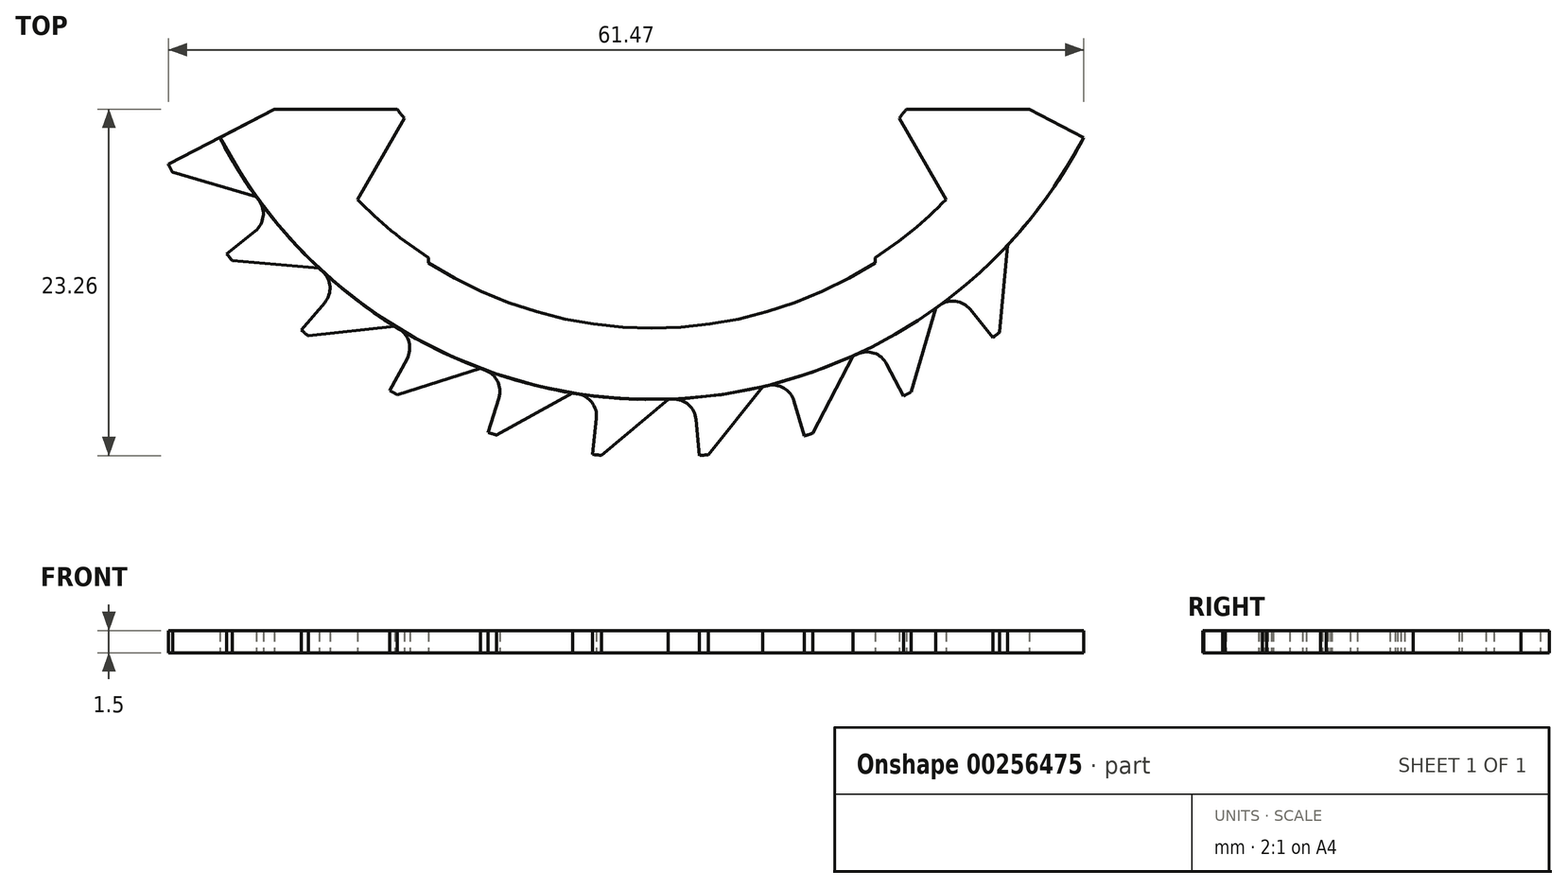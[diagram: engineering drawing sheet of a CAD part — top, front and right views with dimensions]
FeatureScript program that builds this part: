
annotation { "Feature Type Name" : "Feature", "Feature Type Description" : "" }
export const myFeature = defineFeature(function(context is Context, id is Id, definition is map)
    precondition{}
    {
        {
            var Q0;
            Q0=qCreatedBy(makeId("Top.planeOp"),FACE);
            var sketch = newSketch(context, id + "F0", { "sketchPlane" : qUnion([Q0]), "disableImprinting" : false});
            skArc(sketch, "E0", {"start": v(5, -7.72) * mm, "mid": v(5.83, -7.12) * mm, "end": v(6.6, -6.42) * mm});
            skArc(sketch, "E1", {"start": v(-5, -7.84) * mm, "mid": v(0, -9.3) * mm, "end": v(5, -7.84) * mm});
            skArc(sketch, "E2", {"start": v(7.64, -9.51) * mm, "mid": v(7.71, -9.45) * mm, "end": v(7.8, -9.39) * mm});
            skCircle(sketch, "E3", {"center": v(0, 0) * mm, "radius": 10.9 * mm});
            skLineSegment(sketch, "E4", {"start": v(0, 0) * mm, "end": v(-10.82, -5.63) * mm});
            skLineSegment(sketch, "E5", {"start": v(0, 0) * mm, "end": v(9.67, -5.03) * mm});
            skLineSegment(sketch, "E6", {"start": v(0, 0) * mm, "end": v(7.64, -9.51) * mm, "construction": true});
            skLineSegment(sketch, "E7", {"start": v(6.82, -8.5) * mm, "end": v(7.64, -9.51) * mm});
            skLineSegment(sketch, "E8", {"start": v(7.8, -9.39) * mm, "end": v(7.96, -7.45) * mm});
            skLineSegment(sketch, "E9", {"start": v(0, 0) * mm, "end": v(9.35, -7.84) * mm, "construction": true});
            skLineSegment(sketch, "E10.1.0", {"start": v(5.8, -10.73) * mm, "end": v(6.36, -8.86) * mm});
            skArc(sketch, "E10.1.1", {"start": v(5.63, -10.82) * mm, "mid": v(5.72, -10.77) * mm, "end": v(5.8, -10.73) * mm});
            skLineSegment(sketch, "E10.1.2", {"start": v(5.03, -9.67) * mm, "end": v(5.63, -10.82) * mm});
            skLineSegment(sketch, "E10.2.0", {"start": v(3.6, -11.66) * mm, "end": v(4.5, -9.92) * mm});
            skArc(sketch, "E10.2.1", {"start": v(3.41, -11.71) * mm, "mid": v(3.5, -11.68) * mm, "end": v(3.6, -11.66) * mm});
            skLineSegment(sketch, "E10.2.2", {"start": v(3.05, -10.46) * mm, "end": v(3.41, -11.71) * mm});
            skLineSegment(sketch, "E10.3.0", {"start": v(1.26, -12.13) * mm, "end": v(2.48, -10.61) * mm});
            skArc(sketch, "E10.3.1", {"start": v(1.06, -12.15) * mm, "mid": v(1.16, -12.14) * mm, "end": v(1.26, -12.13) * mm});
            skLineSegment(sketch, "E10.3.2", {"start": v(0.95, -10.86) * mm, "end": v(1.06, -12.15) * mm});
            skLineSegment(sketch, "E10.4.0", {"start": v(-1.13, -12.15) * mm, "end": v(0.36, -10.9) * mm});
            skArc(sketch, "E10.4.1", {"start": v(-1.33, -12.13) * mm, "mid": v(-1.23, -12.14) * mm, "end": v(-1.13, -12.15) * mm});
            skLineSegment(sketch, "E10.4.2", {"start": v(-1.19, -10.84) * mm, "end": v(-1.33, -12.13) * mm});
            skLineSegment(sketch, "E10.5.0", {"start": v(-3.48, -11.7) * mm, "end": v(-1.77, -10.76) * mm});
            skArc(sketch, "E10.5.1", {"start": v(-3.67, -11.64) * mm, "mid": v(-3.57, -11.67) * mm, "end": v(-3.48, -11.7) * mm});
            skLineSegment(sketch, "E10.5.2", {"start": v(-3.28, -10.4) * mm, "end": v(-3.67, -11.64) * mm});
            skLineSegment(sketch, "E10.6.0", {"start": v(-5.7, -10.8) * mm, "end": v(-3.83, -10.2) * mm});
            skArc(sketch, "E10.6.1", {"start": v(-5.87, -10.7) * mm, "mid": v(-5.78, -10.74) * mm, "end": v(-5.7, -10.8) * mm});
            skLineSegment(sketch, "E10.6.2", {"start": v(-5.24, -9.56) * mm, "end": v(-5.87, -10.7) * mm});
            skLineSegment(sketch, "E10.7.0", {"start": v(-7.69, -9.47) * mm, "end": v(-5.75, -9.26) * mm});
            skArc(sketch, "E10.7.1", {"start": v(-7.84, -9.35) * mm, "mid": v(-7.77, -9.4) * mm, "end": v(-7.69, -9.47) * mm});
            skLineSegment(sketch, "E10.7.2", {"start": v(-7, -8.35) * mm, "end": v(-7.84, -9.35) * mm});
            skLineSegment(sketch, "E10.8.0", {"start": v(-9.39, -7.8) * mm, "end": v(-7.45, -7.96) * mm});
            skArc(sketch, "E10.8.1", {"start": v(-9.51, -7.64) * mm, "mid": v(-9.45, -7.71) * mm, "end": v(-9.39, -7.8) * mm});
            skLineSegment(sketch, "E10.8.2", {"start": v(-8.5, -6.82) * mm, "end": v(-9.51, -7.64) * mm});
            skLineSegment(sketch, "E10.9.0", {"start": v(-10.73, -5.8) * mm, "end": v(-8.86, -6.36) * mm});
            skArc(sketch, "E10.9.1", {"start": v(-10.82, -5.63) * mm, "mid": v(-10.77, -5.72) * mm, "end": v(-10.73, -5.8) * mm});
            skLineSegment(sketch, "E10.9.2", {"start": v(-9.67, -5.03) * mm, "end": v(-10.82, -5.63) * mm});
            skLineSegment(sketch, "E10.anchor1", {"start": v(0, 0) * mm, "end": v(7.8, -9.39) * mm, "construction": true});
            skLineSegment(sketch, "E10.anchor2", {"start": v(0, 0) * mm, "end": v(-9.58, -5.2) * mm, "construction": true});
            skArc(sketch, "E11", {"start": v(7.13, -8.88) * mm, "mid": v(6.8, -8.7) * mm, "end": v(6.44, -8.8) * mm});
            skArc(sketch, "E12.1.0", {"start": v(5.26, -10.1) * mm, "mid": v(4.98, -9.86) * mm, "end": v(4.6, -9.88) * mm});
            skArc(sketch, "E12.2.0", {"start": v(3.19, -10.93) * mm, "mid": v(2.96, -10.64) * mm, "end": v(2.59, -10.59) * mm});
            skArc(sketch, "E12.3.0", {"start": v(1, -11.35) * mm, "mid": v(0.82, -11.01) * mm, "end": v(0.47, -10.89) * mm});
            skArc(sketch, "E12.4.0", {"start": v(-1.24, -11.32) * mm, "mid": v(-1.34, -10.96) * mm, "end": v(-1.66, -10.77) * mm});
            skArc(sketch, "E12.5.0", {"start": v(-3.42, -10.86) * mm, "mid": v(-3.45, -10.5) * mm, "end": v(-3.73, -10.24) * mm});
            skArc(sketch, "E12.6.0", {"start": v(-5.48, -9.99) * mm, "mid": v(-5.43, -9.62) * mm, "end": v(-5.66, -9.32) * mm});
            skArc(sketch, "E12.7.0", {"start": v(-7.32, -8.72) * mm, "mid": v(-7.2, -8.37) * mm, "end": v(-7.37, -8.03) * mm});
            skArc(sketch, "E12.8.0", {"start": v(-8.88, -7.13) * mm, "mid": v(-8.7, -6.8) * mm, "end": v(-8.8, -6.44) * mm});
            skLineSegment(sketch, "E12.anchor1", {"start": v(6.44, -8.8) * mm, "end": v(0, 0) * mm, "construction": true});
            skLineSegment(sketch, "E12.anchor2", {"start": v(0, 0) * mm, "end": v(-8.8, -6.44) * mm, "construction": true});
            skCircle(sketch, "E13", {"center": v(0, 0) * mm, "radius": 12.2 * mm, "construction": true});
            skLineSegment(sketch, "E14", {"start": v(-8.45, -4.4) * mm, "end": v(-5.7, -4.4) * mm});
            skPoint(sketch, "E15", {"position": v(0, 5) * mm});
            skLineSegment(sketch, "E16", {"start": v(0, 5) * mm, "end": v(-6.6, -6.42) * mm});
            skLineSegment(sketch, "E17", {"start": v(0, 5) * mm, "end": v(6.6, -6.42) * mm});
            skLineSegment(sketch, "E18", {"start": v(-5, -7.72) * mm, "end": v(-5, -7.84) * mm});
            skLineSegment(sketch, "E19", {"start": v(5, -7.72) * mm, "end": v(5, -7.84) * mm});
            skArc(sketch, "E20.trimOffspring", {"start": v(5.52, -4.63) * mm, "mid": v(5.6, -4.51) * mm, "end": v(5.7, -4.4) * mm});
            skLineSegment(sketch, "E21.trimOffspring", {"start": v(5.7, -4.4) * mm, "end": v(8.45, -4.4) * mm});
            skLineSegment(sketch, "E22.trimOffspring", {"start": v(-9.58, -5.2) * mm, "end": v(-10.73, -5.8) * mm, "construction": true});
            skArc(sketch, "E23", {"start": v(-5.7, -4.4) * mm, "mid": v(-5.62, -4.5) * mm, "end": v(-5.54, -4.6) * mm});
            skArc(sketch, "E24", {"start": v(-6.6, -6.42) * mm, "mid": v(-5.83, -7.12) * mm, "end": v(-5, -7.72) * mm});
            skSolve(sketch);
        }
        {
            var Q0;
            {var subQ6=sQuery(id+"F0.wireOp",EDGE,"E0");Q0=makeQuery(id+"F0.imprint","IMPRINT",FACE,{"disambiguationData":[TD([[makeQuery(id+"F0.imprint","IMPRINT",EDGE,{"derivedFrom":subQ6}),-1.0]])]});}
            var Q1;
            {var subQ1=sQuery(id+"F0.wireOp",EDGE,"E10.9.0");Q1=makeQuery(id+"F0.imprint","IMPRINT",FACE,{"disambiguationData":[TD([[makeQuery(id+"F0.imprint","IMPRINT",EDGE,{"derivedFrom":subQ1}),1.0]])]});}
            var Q2;
            {var subQ5=sQuery(id+"F0.wireOp",EDGE,"E10.8.0");Q2=makeQuery(id+"F0.imprint","IMPRINT",FACE,{"disambiguationData":[TD([[makeQuery(id+"F0.imprint","IMPRINT",EDGE,{"derivedFrom":subQ5}),1.0]])]});}
            var Q3;
            {var subQ5=sQuery(id+"F0.wireOp",EDGE,"E10.7.0");Q3=makeQuery(id+"F0.imprint","IMPRINT",FACE,{"disambiguationData":[TD([[makeQuery(id+"F0.imprint","IMPRINT",EDGE,{"derivedFrom":subQ5}),1.0]])]});}
            var Q4;
            {var subQ5=sQuery(id+"F0.wireOp",EDGE,"E10.6.0");Q4=makeQuery(id+"F0.imprint","IMPRINT",FACE,{"disambiguationData":[TD([[makeQuery(id+"F0.imprint","IMPRINT",EDGE,{"derivedFrom":subQ5}),1.0]])]});}
            var Q5;
            {var subQ5=sQuery(id+"F0.wireOp",EDGE,"E10.5.0");Q5=makeQuery(id+"F0.imprint","IMPRINT",FACE,{"disambiguationData":[TD([[makeQuery(id+"F0.imprint","IMPRINT",EDGE,{"derivedFrom":subQ5}),1.0]])]});}
            var Q6;
            {var subQ5=sQuery(id+"F0.wireOp",EDGE,"E10.4.0");Q6=makeQuery(id+"F0.imprint","IMPRINT",FACE,{"disambiguationData":[TD([[makeQuery(id+"F0.imprint","IMPRINT",EDGE,{"derivedFrom":subQ5}),1.0]])]});}
            var Q7;
            {var subQ5=sQuery(id+"F0.wireOp",EDGE,"E10.3.0");Q7=makeQuery(id+"F0.imprint","IMPRINT",FACE,{"disambiguationData":[TD([[makeQuery(id+"F0.imprint","IMPRINT",EDGE,{"derivedFrom":subQ5}),1.0]])]});}
            var Q8;
            {var subQ2=sQuery(id+"F0.wireOp",EDGE,"E2");Q8=makeQuery(id+"F0.imprint","IMPRINT",FACE,{"disambiguationData":[TD([[makeQuery(id+"F0.imprint","IMPRINT",EDGE,{"derivedFrom":subQ2}),1.0]])]});}
            var Q9;
            {var subQ5=sQuery(id+"F0.wireOp",EDGE,"E10.1.0");Q9=makeQuery(id+"F0.imprint","IMPRINT",FACE,{"disambiguationData":[TD([[makeQuery(id+"F0.imprint","IMPRINT",EDGE,{"derivedFrom":subQ5}),1.0]])]});}
            var Q10;
            {var subQ5=sQuery(id+"F0.wireOp",EDGE,"E10.2.0");Q10=makeQuery(id+"F0.imprint","IMPRINT",FACE,{"disambiguationData":[TD([[makeQuery(id+"F0.imprint","IMPRINT",EDGE,{"derivedFrom":subQ5}),1.0]])]});}
            var Q11;
            {var subQ1=sQuery(id+"F0.wireOp",EDGE,"E11");Q11=makeQuery(id+"F0.imprint","IMPRINT",FACE,{"disambiguationData":[TD([[makeQuery(id+"F0.imprint","IMPRINT",EDGE,{"derivedFrom":subQ1}),-1.0]])]});}
            var Q12;
            {var subQ0=sQuery(id+"F0.wireOp",EDGE,"E12.1.0");Q12=makeQuery(id+"F0.imprint","IMPRINT",FACE,{"disambiguationData":[TD([[makeQuery(id+"F0.imprint","IMPRINT",EDGE,{"derivedFrom":subQ0}),-1.0]])]});}
            var Q13;
            {var subQ0=sQuery(id+"F0.wireOp",EDGE,"E12.2.0");Q13=makeQuery(id+"F0.imprint","IMPRINT",FACE,{"disambiguationData":[TD([[makeQuery(id+"F0.imprint","IMPRINT",EDGE,{"derivedFrom":subQ0}),-1.0]])]});}
            var Q14;
            {var subQ0=sQuery(id+"F0.wireOp",EDGE,"E12.3.0");Q14=makeQuery(id+"F0.imprint","IMPRINT",FACE,{"disambiguationData":[TD([[makeQuery(id+"F0.imprint","IMPRINT",EDGE,{"derivedFrom":subQ0}),-1.0]])]});}
            var Q15;
            {var subQ0=sQuery(id+"F0.wireOp",EDGE,"E12.4.0");Q15=makeQuery(id+"F0.imprint","IMPRINT",FACE,{"disambiguationData":[TD([[makeQuery(id+"F0.imprint","IMPRINT",EDGE,{"derivedFrom":subQ0}),-1.0]])]});}
            var Q16;
            {var subQ0=sQuery(id+"F0.wireOp",EDGE,"E12.5.0");Q16=makeQuery(id+"F0.imprint","IMPRINT",FACE,{"disambiguationData":[TD([[makeQuery(id+"F0.imprint","IMPRINT",EDGE,{"derivedFrom":subQ0}),-1.0]])]});}
            var Q17;
            {var subQ0=sQuery(id+"F0.wireOp",EDGE,"E12.6.0");Q17=makeQuery(id+"F0.imprint","IMPRINT",FACE,{"disambiguationData":[TD([[makeQuery(id+"F0.imprint","IMPRINT",EDGE,{"derivedFrom":subQ0}),-1.0]])]});}
            var Q18;
            {var subQ0=sQuery(id+"F0.wireOp",EDGE,"E12.8.0");Q18=makeQuery(id+"F0.imprint","IMPRINT",FACE,{"disambiguationData":[TD([[makeQuery(id+"F0.imprint","IMPRINT",EDGE,{"derivedFrom":subQ0}),-1.0]])]});}
            var Q19;
            {var subQ0=sQuery(id+"F0.wireOp",EDGE,"E12.7.0");Q19=makeQuery(id+"F0.imprint","IMPRINT",FACE,{"disambiguationData":[TD([[makeQuery(id+"F0.imprint","IMPRINT",EDGE,{"derivedFrom":subQ0}),-1.0]])]});}
            extrude(context, id + "F1", {"entities" : qUnion([Q0, Q1, Q2, Q3, Q4, Q5, Q6, Q7, Q8, Q9, Q10, Q11, Q12, Q13, Q14, Q15, Q16, Q17, Q18, Q19]), "depth" : 0.5 * mm});
        }
        {
            var Q0;
            {var subQ6=sQuery(id+"F0.wireOp",EDGE,"E0");Q0=makeQuery(id+"F0.imprint","IMPRINT",FACE,{"disambiguationData":[TD([[makeQuery(id+"F0.imprint","IMPRINT",EDGE,{"derivedFrom":subQ6}),-1.0]])]});}
            var Q1;
            {var subQ2=sQuery(id+"F0.wireOp",EDGE,"E2");Q1=makeQuery(id+"F0.imprint","IMPRINT",FACE,{"disambiguationData":[TD([[makeQuery(id+"F0.imprint","IMPRINT",EDGE,{"derivedFrom":subQ2}),1.0]])]});}
            var Q2;
            {var subQ1=sQuery(id+"F0.wireOp",EDGE,"E11");Q2=makeQuery(id+"F0.imprint","IMPRINT",FACE,{"disambiguationData":[TD([[makeQuery(id+"F0.imprint","IMPRINT",EDGE,{"derivedFrom":subQ1}),-1.0]])]});}
            var Q3;
            {var subQ5=sQuery(id+"F0.wireOp",EDGE,"E10.1.0");Q3=makeQuery(id+"F0.imprint","IMPRINT",FACE,{"disambiguationData":[TD([[makeQuery(id+"F0.imprint","IMPRINT",EDGE,{"derivedFrom":subQ5}),1.0]])]});}
            var Q4;
            {var subQ0=sQuery(id+"F0.wireOp",EDGE,"E12.1.0");Q4=makeQuery(id+"F0.imprint","IMPRINT",FACE,{"disambiguationData":[TD([[makeQuery(id+"F0.imprint","IMPRINT",EDGE,{"derivedFrom":subQ0}),-1.0]])]});}
            var Q5;
            {var subQ5=sQuery(id+"F0.wireOp",EDGE,"E10.2.0");Q5=makeQuery(id+"F0.imprint","IMPRINT",FACE,{"disambiguationData":[TD([[makeQuery(id+"F0.imprint","IMPRINT",EDGE,{"derivedFrom":subQ5}),1.0]])]});}
            var Q6;
            {var subQ0=sQuery(id+"F0.wireOp",EDGE,"E12.2.0");Q6=makeQuery(id+"F0.imprint","IMPRINT",FACE,{"disambiguationData":[TD([[makeQuery(id+"F0.imprint","IMPRINT",EDGE,{"derivedFrom":subQ0}),-1.0]])]});}
            var Q7;
            {var subQ5=sQuery(id+"F0.wireOp",EDGE,"E10.3.0");Q7=makeQuery(id+"F0.imprint","IMPRINT",FACE,{"disambiguationData":[TD([[makeQuery(id+"F0.imprint","IMPRINT",EDGE,{"derivedFrom":subQ5}),1.0]])]});}
            var Q8;
            {var subQ0=sQuery(id+"F0.wireOp",EDGE,"E12.3.0");Q8=makeQuery(id+"F0.imprint","IMPRINT",FACE,{"disambiguationData":[TD([[makeQuery(id+"F0.imprint","IMPRINT",EDGE,{"derivedFrom":subQ0}),-1.0]])]});}
            var Q9;
            {var subQ5=sQuery(id+"F0.wireOp",EDGE,"E10.4.0");Q9=makeQuery(id+"F0.imprint","IMPRINT",FACE,{"disambiguationData":[TD([[makeQuery(id+"F0.imprint","IMPRINT",EDGE,{"derivedFrom":subQ5}),1.0]])]});}
            var Q10;
            {var subQ0=sQuery(id+"F0.wireOp",EDGE,"E12.4.0");Q10=makeQuery(id+"F0.imprint","IMPRINT",FACE,{"disambiguationData":[TD([[makeQuery(id+"F0.imprint","IMPRINT",EDGE,{"derivedFrom":subQ0}),-1.0]])]});}
            var Q11;
            {var subQ5=sQuery(id+"F0.wireOp",EDGE,"E10.5.0");Q11=makeQuery(id+"F0.imprint","IMPRINT",FACE,{"disambiguationData":[TD([[makeQuery(id+"F0.imprint","IMPRINT",EDGE,{"derivedFrom":subQ5}),1.0]])]});}
            var Q12;
            {var subQ0=sQuery(id+"F0.wireOp",EDGE,"E12.5.0");Q12=makeQuery(id+"F0.imprint","IMPRINT",FACE,{"disambiguationData":[TD([[makeQuery(id+"F0.imprint","IMPRINT",EDGE,{"derivedFrom":subQ0}),-1.0]])]});}
            var Q13;
            {var subQ5=sQuery(id+"F0.wireOp",EDGE,"E10.6.0");Q13=makeQuery(id+"F0.imprint","IMPRINT",FACE,{"disambiguationData":[TD([[makeQuery(id+"F0.imprint","IMPRINT",EDGE,{"derivedFrom":subQ5}),1.0]])]});}
            var Q14;
            {var subQ0=sQuery(id+"F0.wireOp",EDGE,"E12.6.0");Q14=makeQuery(id+"F0.imprint","IMPRINT",FACE,{"disambiguationData":[TD([[makeQuery(id+"F0.imprint","IMPRINT",EDGE,{"derivedFrom":subQ0}),-1.0]])]});}
            var Q15;
            {var subQ5=sQuery(id+"F0.wireOp",EDGE,"E10.7.0");Q15=makeQuery(id+"F0.imprint","IMPRINT",FACE,{"disambiguationData":[TD([[makeQuery(id+"F0.imprint","IMPRINT",EDGE,{"derivedFrom":subQ5}),1.0]])]});}
            var Q16;
            {var subQ0=sQuery(id+"F0.wireOp",EDGE,"E12.7.0");Q16=makeQuery(id+"F0.imprint","IMPRINT",FACE,{"disambiguationData":[TD([[makeQuery(id+"F0.imprint","IMPRINT",EDGE,{"derivedFrom":subQ0}),-1.0]])]});}
            var Q17;
            {var subQ5=sQuery(id+"F0.wireOp",EDGE,"E10.8.0");Q17=makeQuery(id+"F0.imprint","IMPRINT",FACE,{"disambiguationData":[TD([[makeQuery(id+"F0.imprint","IMPRINT",EDGE,{"derivedFrom":subQ5}),1.0]])]});}
            var Q18;
            {var subQ0=sQuery(id+"F0.wireOp",EDGE,"E12.8.0");Q18=makeQuery(id+"F0.imprint","IMPRINT",FACE,{"disambiguationData":[TD([[makeQuery(id+"F0.imprint","IMPRINT",EDGE,{"derivedFrom":subQ0}),-1.0]])]});}
            extrude(context, id + "F2", {"entities" : qUnion([Q0, Q1, Q2, Q3, Q4, Q5, Q6, Q7, Q8, Q9, Q10, Q11, Q12, Q13, Q14, Q15, Q16, Q17, Q18]), "depth" : 0.5 * mm});
        }
        {
            var Q0;
            {var subQ6=sQuery(id+"F0.wireOp",EDGE,"E0");Q0=makeQuery(id+"F0.imprint","IMPRINT",FACE,{"disambiguationData":[TD([[makeQuery(id+"F0.imprint","IMPRINT",EDGE,{"derivedFrom":subQ6}),-1.0]])]});}
            var Q1;
            {var subQ5=sQuery(id+"F0.wireOp",EDGE,"E10.7.0");Q1=makeQuery(id+"F0.imprint","IMPRINT",FACE,{"disambiguationData":[TD([[makeQuery(id+"F0.imprint","IMPRINT",EDGE,{"derivedFrom":subQ5}),1.0]])]});}
            var Q2;
            {var subQ0=sQuery(id+"F0.wireOp",EDGE,"E12.6.0");Q2=makeQuery(id+"F0.imprint","IMPRINT",FACE,{"disambiguationData":[TD([[makeQuery(id+"F0.imprint","IMPRINT",EDGE,{"derivedFrom":subQ0}),-1.0]])]});}
            var Q3;
            {var subQ5=sQuery(id+"F0.wireOp",EDGE,"E10.6.0");Q3=makeQuery(id+"F0.imprint","IMPRINT",FACE,{"disambiguationData":[TD([[makeQuery(id+"F0.imprint","IMPRINT",EDGE,{"derivedFrom":subQ5}),1.0]])]});}
            var Q4;
            {var subQ0=sQuery(id+"F0.wireOp",EDGE,"E12.5.0");Q4=makeQuery(id+"F0.imprint","IMPRINT",FACE,{"disambiguationData":[TD([[makeQuery(id+"F0.imprint","IMPRINT",EDGE,{"derivedFrom":subQ0}),-1.0]])]});}
            var Q5;
            {var subQ5=sQuery(id+"F0.wireOp",EDGE,"E10.5.0");Q5=makeQuery(id+"F0.imprint","IMPRINT",FACE,{"disambiguationData":[TD([[makeQuery(id+"F0.imprint","IMPRINT",EDGE,{"derivedFrom":subQ5}),1.0]])]});}
            var Q6;
            {var subQ0=sQuery(id+"F0.wireOp",EDGE,"E12.4.0");Q6=makeQuery(id+"F0.imprint","IMPRINT",FACE,{"disambiguationData":[TD([[makeQuery(id+"F0.imprint","IMPRINT",EDGE,{"derivedFrom":subQ0}),-1.0]])]});}
            var Q7;
            {var subQ5=sQuery(id+"F0.wireOp",EDGE,"E10.4.0");Q7=makeQuery(id+"F0.imprint","IMPRINT",FACE,{"disambiguationData":[TD([[makeQuery(id+"F0.imprint","IMPRINT",EDGE,{"derivedFrom":subQ5}),1.0]])]});}
            var Q8;
            {var subQ0=sQuery(id+"F0.wireOp",EDGE,"E12.3.0");Q8=makeQuery(id+"F0.imprint","IMPRINT",FACE,{"disambiguationData":[TD([[makeQuery(id+"F0.imprint","IMPRINT",EDGE,{"derivedFrom":subQ0}),-1.0]])]});}
            var Q9;
            {var subQ5=sQuery(id+"F0.wireOp",EDGE,"E10.3.0");Q9=makeQuery(id+"F0.imprint","IMPRINT",FACE,{"disambiguationData":[TD([[makeQuery(id+"F0.imprint","IMPRINT",EDGE,{"derivedFrom":subQ5}),1.0]])]});}
            var Q10;
            {var subQ0=sQuery(id+"F0.wireOp",EDGE,"E12.2.0");Q10=makeQuery(id+"F0.imprint","IMPRINT",FACE,{"disambiguationData":[TD([[makeQuery(id+"F0.imprint","IMPRINT",EDGE,{"derivedFrom":subQ0}),-1.0]])]});}
            var Q11;
            {var subQ5=sQuery(id+"F0.wireOp",EDGE,"E10.2.0");Q11=makeQuery(id+"F0.imprint","IMPRINT",FACE,{"disambiguationData":[TD([[makeQuery(id+"F0.imprint","IMPRINT",EDGE,{"derivedFrom":subQ5}),1.0]])]});}
            var Q12;
            {var subQ0=sQuery(id+"F0.wireOp",EDGE,"E12.1.0");Q12=makeQuery(id+"F0.imprint","IMPRINT",FACE,{"disambiguationData":[TD([[makeQuery(id+"F0.imprint","IMPRINT",EDGE,{"derivedFrom":subQ0}),-1.0]])]});}
            var Q13;
            {var subQ5=sQuery(id+"F0.wireOp",EDGE,"E10.1.0");Q13=makeQuery(id+"F0.imprint","IMPRINT",FACE,{"disambiguationData":[TD([[makeQuery(id+"F0.imprint","IMPRINT",EDGE,{"derivedFrom":subQ5}),1.0]])]});}
            var Q14;
            {var subQ2=sQuery(id+"F0.wireOp",EDGE,"E2");Q14=makeQuery(id+"F0.imprint","IMPRINT",FACE,{"disambiguationData":[TD([[makeQuery(id+"F0.imprint","IMPRINT",EDGE,{"derivedFrom":subQ2}),1.0]])]});}
            var Q15;
            {var subQ1=sQuery(id+"F0.wireOp",EDGE,"E11");Q15=makeQuery(id+"F0.imprint","IMPRINT",FACE,{"disambiguationData":[TD([[makeQuery(id+"F0.imprint","IMPRINT",EDGE,{"derivedFrom":subQ1}),-1.0]])]});}
            var Q16;
            {var subQ0=sQuery(id+"F0.wireOp",EDGE,"E12.7.0");Q16=makeQuery(id+"F0.imprint","IMPRINT",FACE,{"disambiguationData":[TD([[makeQuery(id+"F0.imprint","IMPRINT",EDGE,{"derivedFrom":subQ0}),-1.0]])]});}
            extrude(context, id + "F3", {"entities" : qUnion([Q0, Q1, Q2, Q3, Q4, Q5, Q6, Q7, Q8, Q9, Q10, Q11, Q12, Q13, Q14, Q15, Q16]), "depth" : 0.5 * mm});
        }
        {
            var Q0;
            {var subQ2=sQuery(id+"F0.wireOp",EDGE,"E2");Q0=makeQuery(id+"F0.imprint","IMPRINT",FACE,{"disambiguationData":[TD([[makeQuery(id+"F0.imprint","IMPRINT",EDGE,{"derivedFrom":subQ2}),1.0]])]});}
            var Q1;
            {var subQ1=sQuery(id+"F0.wireOp",EDGE,"E11");Q1=makeQuery(id+"F0.imprint","IMPRINT",FACE,{"disambiguationData":[TD([[makeQuery(id+"F0.imprint","IMPRINT",EDGE,{"derivedFrom":subQ1}),-1.0]])]});}
            var Q2;
            {var subQ5=sQuery(id+"F0.wireOp",EDGE,"E10.1.0");Q2=makeQuery(id+"F0.imprint","IMPRINT",FACE,{"disambiguationData":[TD([[makeQuery(id+"F0.imprint","IMPRINT",EDGE,{"derivedFrom":subQ5}),1.0]])]});}
            var Q3;
            {var subQ0=sQuery(id+"F0.wireOp",EDGE,"E12.1.0");Q3=makeQuery(id+"F0.imprint","IMPRINT",FACE,{"disambiguationData":[TD([[makeQuery(id+"F0.imprint","IMPRINT",EDGE,{"derivedFrom":subQ0}),-1.0]])]});}
            var Q4;
            {var subQ5=sQuery(id+"F0.wireOp",EDGE,"E10.2.0");Q4=makeQuery(id+"F0.imprint","IMPRINT",FACE,{"disambiguationData":[TD([[makeQuery(id+"F0.imprint","IMPRINT",EDGE,{"derivedFrom":subQ5}),1.0]])]});}
            var Q5;
            {var subQ0=sQuery(id+"F0.wireOp",EDGE,"E12.2.0");Q5=makeQuery(id+"F0.imprint","IMPRINT",FACE,{"disambiguationData":[TD([[makeQuery(id+"F0.imprint","IMPRINT",EDGE,{"derivedFrom":subQ0}),-1.0]])]});}
            var Q6;
            {var subQ5=sQuery(id+"F0.wireOp",EDGE,"E10.3.0");Q6=makeQuery(id+"F0.imprint","IMPRINT",FACE,{"disambiguationData":[TD([[makeQuery(id+"F0.imprint","IMPRINT",EDGE,{"derivedFrom":subQ5}),1.0]])]});}
            var Q7;
            {var subQ0=sQuery(id+"F0.wireOp",EDGE,"E12.3.0");Q7=makeQuery(id+"F0.imprint","IMPRINT",FACE,{"disambiguationData":[TD([[makeQuery(id+"F0.imprint","IMPRINT",EDGE,{"derivedFrom":subQ0}),-1.0]])]});}
            var Q8;
            {var subQ5=sQuery(id+"F0.wireOp",EDGE,"E10.4.0");Q8=makeQuery(id+"F0.imprint","IMPRINT",FACE,{"disambiguationData":[TD([[makeQuery(id+"F0.imprint","IMPRINT",EDGE,{"derivedFrom":subQ5}),1.0]])]});}
            var Q9;
            {var subQ0=sQuery(id+"F0.wireOp",EDGE,"E12.4.0");Q9=makeQuery(id+"F0.imprint","IMPRINT",FACE,{"disambiguationData":[TD([[makeQuery(id+"F0.imprint","IMPRINT",EDGE,{"derivedFrom":subQ0}),-1.0]])]});}
            var Q10;
            {var subQ5=sQuery(id+"F0.wireOp",EDGE,"E10.5.0");Q10=makeQuery(id+"F0.imprint","IMPRINT",FACE,{"disambiguationData":[TD([[makeQuery(id+"F0.imprint","IMPRINT",EDGE,{"derivedFrom":subQ5}),1.0]])]});}
            var Q11;
            {var subQ0=sQuery(id+"F0.wireOp",EDGE,"E12.5.0");Q11=makeQuery(id+"F0.imprint","IMPRINT",FACE,{"disambiguationData":[TD([[makeQuery(id+"F0.imprint","IMPRINT",EDGE,{"derivedFrom":subQ0}),-1.0]])]});}
            var Q12;
            {var subQ5=sQuery(id+"F0.wireOp",EDGE,"E10.6.0");Q12=makeQuery(id+"F0.imprint","IMPRINT",FACE,{"disambiguationData":[TD([[makeQuery(id+"F0.imprint","IMPRINT",EDGE,{"derivedFrom":subQ5}),1.0]])]});}
            var Q13;
            {var subQ6=sQuery(id+"F0.wireOp",EDGE,"E0");Q13=makeQuery(id+"F0.imprint","IMPRINT",FACE,{"disambiguationData":[TD([[makeQuery(id+"F0.imprint","IMPRINT",EDGE,{"derivedFrom":subQ6}),-1.0]])]});}
            var Q14;
            {var subQ0=sQuery(id+"F0.wireOp",EDGE,"E12.6.0");Q14=makeQuery(id+"F0.imprint","IMPRINT",FACE,{"disambiguationData":[TD([[makeQuery(id+"F0.imprint","IMPRINT",EDGE,{"derivedFrom":subQ0}),-1.0]])]});}
            extrude(context, id + "F4", {"entities" : qUnion([Q0, Q1, Q2, Q3, Q4, Q5, Q6, Q7, Q8, Q9, Q10, Q11, Q12, Q13, Q14]), "depth" : 0.5 * mm});
        }
        {
            var Q0;
            {var subQ6=sQuery(id+"F0.wireOp",EDGE,"E0");Q0=makeQuery(id+"F0.imprint","IMPRINT",FACE,{"disambiguationData":[TD([[makeQuery(id+"F0.imprint","IMPRINT",EDGE,{"derivedFrom":subQ6}),-1.0]])]});}
            var Q1;
            {var subQ5=sQuery(id+"F0.wireOp",EDGE,"E10.5.0");Q1=makeQuery(id+"F0.imprint","IMPRINT",FACE,{"disambiguationData":[TD([[makeQuery(id+"F0.imprint","IMPRINT",EDGE,{"derivedFrom":subQ5}),1.0]])]});}
            var Q2;
            {var subQ0=sQuery(id+"F0.wireOp",EDGE,"E12.4.0");Q2=makeQuery(id+"F0.imprint","IMPRINT",FACE,{"disambiguationData":[TD([[makeQuery(id+"F0.imprint","IMPRINT",EDGE,{"derivedFrom":subQ0}),-1.0]])]});}
            var Q3;
            {var subQ5=sQuery(id+"F0.wireOp",EDGE,"E10.4.0");Q3=makeQuery(id+"F0.imprint","IMPRINT",FACE,{"disambiguationData":[TD([[makeQuery(id+"F0.imprint","IMPRINT",EDGE,{"derivedFrom":subQ5}),1.0]])]});}
            var Q4;
            {var subQ0=sQuery(id+"F0.wireOp",EDGE,"E12.3.0");Q4=makeQuery(id+"F0.imprint","IMPRINT",FACE,{"disambiguationData":[TD([[makeQuery(id+"F0.imprint","IMPRINT",EDGE,{"derivedFrom":subQ0}),-1.0]])]});}
            var Q5;
            {var subQ5=sQuery(id+"F0.wireOp",EDGE,"E10.3.0");Q5=makeQuery(id+"F0.imprint","IMPRINT",FACE,{"disambiguationData":[TD([[makeQuery(id+"F0.imprint","IMPRINT",EDGE,{"derivedFrom":subQ5}),1.0]])]});}
            var Q6;
            {var subQ0=sQuery(id+"F0.wireOp",EDGE,"E12.2.0");Q6=makeQuery(id+"F0.imprint","IMPRINT",FACE,{"disambiguationData":[TD([[makeQuery(id+"F0.imprint","IMPRINT",EDGE,{"derivedFrom":subQ0}),-1.0]])]});}
            var Q7;
            {var subQ5=sQuery(id+"F0.wireOp",EDGE,"E10.2.0");Q7=makeQuery(id+"F0.imprint","IMPRINT",FACE,{"disambiguationData":[TD([[makeQuery(id+"F0.imprint","IMPRINT",EDGE,{"derivedFrom":subQ5}),1.0]])]});}
            var Q8;
            {var subQ0=sQuery(id+"F0.wireOp",EDGE,"E12.1.0");Q8=makeQuery(id+"F0.imprint","IMPRINT",FACE,{"disambiguationData":[TD([[makeQuery(id+"F0.imprint","IMPRINT",EDGE,{"derivedFrom":subQ0}),-1.0]])]});}
            var Q9;
            {var subQ5=sQuery(id+"F0.wireOp",EDGE,"E10.1.0");Q9=makeQuery(id+"F0.imprint","IMPRINT",FACE,{"disambiguationData":[TD([[makeQuery(id+"F0.imprint","IMPRINT",EDGE,{"derivedFrom":subQ5}),1.0]])]});}
            var Q10;
            {var subQ1=sQuery(id+"F0.wireOp",EDGE,"E11");Q10=makeQuery(id+"F0.imprint","IMPRINT",FACE,{"disambiguationData":[TD([[makeQuery(id+"F0.imprint","IMPRINT",EDGE,{"derivedFrom":subQ1}),-1.0]])]});}
            var Q11;
            {var subQ2=sQuery(id+"F0.wireOp",EDGE,"E2");Q11=makeQuery(id+"F0.imprint","IMPRINT",FACE,{"disambiguationData":[TD([[makeQuery(id+"F0.imprint","IMPRINT",EDGE,{"derivedFrom":subQ2}),1.0]])]});}
            var Q12;
            {var subQ0=sQuery(id+"F0.wireOp",EDGE,"E12.5.0");Q12=makeQuery(id+"F0.imprint","IMPRINT",FACE,{"disambiguationData":[TD([[makeQuery(id+"F0.imprint","IMPRINT",EDGE,{"derivedFrom":subQ0}),-1.0]])]});}
            extrude(context, id + "F5", {"entities" : qUnion([Q0, Q1, Q2, Q3, Q4, Q5, Q6, Q7, Q8, Q9, Q10, Q11, Q12]), "depth" : 0.5 * mm});
        }
        {
            var Q0;
            {var subQ5=sQuery(id+"F0.wireOp",EDGE,"E10.4.0");Q0=makeQuery(id+"F0.imprint","IMPRINT",FACE,{"disambiguationData":[TD([[makeQuery(id+"F0.imprint","IMPRINT",EDGE,{"derivedFrom":subQ5}),1.0]])]});}
            var Q1;
            {var subQ6=sQuery(id+"F0.wireOp",EDGE,"E0");Q1=makeQuery(id+"F0.imprint","IMPRINT",FACE,{"disambiguationData":[TD([[makeQuery(id+"F0.imprint","IMPRINT",EDGE,{"derivedFrom":subQ6}),-1.0]])]});}
            var Q2;
            {var subQ0=sQuery(id+"F0.wireOp",EDGE,"E12.3.0");Q2=makeQuery(id+"F0.imprint","IMPRINT",FACE,{"disambiguationData":[TD([[makeQuery(id+"F0.imprint","IMPRINT",EDGE,{"derivedFrom":subQ0}),-1.0]])]});}
            var Q3;
            {var subQ5=sQuery(id+"F0.wireOp",EDGE,"E10.3.0");Q3=makeQuery(id+"F0.imprint","IMPRINT",FACE,{"disambiguationData":[TD([[makeQuery(id+"F0.imprint","IMPRINT",EDGE,{"derivedFrom":subQ5}),1.0]])]});}
            var Q4;
            {var subQ0=sQuery(id+"F0.wireOp",EDGE,"E12.2.0");Q4=makeQuery(id+"F0.imprint","IMPRINT",FACE,{"disambiguationData":[TD([[makeQuery(id+"F0.imprint","IMPRINT",EDGE,{"derivedFrom":subQ0}),-1.0]])]});}
            var Q5;
            {var subQ5=sQuery(id+"F0.wireOp",EDGE,"E10.2.0");Q5=makeQuery(id+"F0.imprint","IMPRINT",FACE,{"disambiguationData":[TD([[makeQuery(id+"F0.imprint","IMPRINT",EDGE,{"derivedFrom":subQ5}),1.0]])]});}
            var Q6;
            {var subQ0=sQuery(id+"F0.wireOp",EDGE,"E12.1.0");Q6=makeQuery(id+"F0.imprint","IMPRINT",FACE,{"disambiguationData":[TD([[makeQuery(id+"F0.imprint","IMPRINT",EDGE,{"derivedFrom":subQ0}),-1.0]])]});}
            var Q7;
            {var subQ5=sQuery(id+"F0.wireOp",EDGE,"E10.1.0");Q7=makeQuery(id+"F0.imprint","IMPRINT",FACE,{"disambiguationData":[TD([[makeQuery(id+"F0.imprint","IMPRINT",EDGE,{"derivedFrom":subQ5}),1.0]])]});}
            var Q8;
            {var subQ1=sQuery(id+"F0.wireOp",EDGE,"E11");Q8=makeQuery(id+"F0.imprint","IMPRINT",FACE,{"disambiguationData":[TD([[makeQuery(id+"F0.imprint","IMPRINT",EDGE,{"derivedFrom":subQ1}),-1.0]])]});}
            var Q9;
            {var subQ2=sQuery(id+"F0.wireOp",EDGE,"E2");Q9=makeQuery(id+"F0.imprint","IMPRINT",FACE,{"disambiguationData":[TD([[makeQuery(id+"F0.imprint","IMPRINT",EDGE,{"derivedFrom":subQ2}),1.0]])]});}
            var Q10;
            {var subQ0=sQuery(id+"F0.wireOp",EDGE,"E12.4.0");Q10=makeQuery(id+"F0.imprint","IMPRINT",FACE,{"disambiguationData":[TD([[makeQuery(id+"F0.imprint","IMPRINT",EDGE,{"derivedFrom":subQ0}),-1.0]])]});}
            extrude(context, id + "F6", {"entities" : qUnion([Q0, Q1, Q2, Q3, Q4, Q5, Q6, Q7, Q8, Q9, Q10]), "depth" : 0.5 * mm});
        }
        {
            var Q0;
            {var subQ6=sQuery(id+"F0.wireOp",EDGE,"E0");Q0=makeQuery(id+"F0.imprint","IMPRINT",FACE,{"disambiguationData":[TD([[makeQuery(id+"F0.imprint","IMPRINT",EDGE,{"derivedFrom":subQ6}),-1.0]])]});}
            var Q1;
            {var subQ5=sQuery(id+"F0.wireOp",EDGE,"E10.3.0");Q1=makeQuery(id+"F0.imprint","IMPRINT",FACE,{"disambiguationData":[TD([[makeQuery(id+"F0.imprint","IMPRINT",EDGE,{"derivedFrom":subQ5}),1.0]])]});}
            var Q2;
            {var subQ0=sQuery(id+"F0.wireOp",EDGE,"E12.2.0");Q2=makeQuery(id+"F0.imprint","IMPRINT",FACE,{"disambiguationData":[TD([[makeQuery(id+"F0.imprint","IMPRINT",EDGE,{"derivedFrom":subQ0}),-1.0]])]});}
            var Q3;
            {var subQ5=sQuery(id+"F0.wireOp",EDGE,"E10.2.0");Q3=makeQuery(id+"F0.imprint","IMPRINT",FACE,{"disambiguationData":[TD([[makeQuery(id+"F0.imprint","IMPRINT",EDGE,{"derivedFrom":subQ5}),1.0]])]});}
            var Q4;
            {var subQ0=sQuery(id+"F0.wireOp",EDGE,"E12.1.0");Q4=makeQuery(id+"F0.imprint","IMPRINT",FACE,{"disambiguationData":[TD([[makeQuery(id+"F0.imprint","IMPRINT",EDGE,{"derivedFrom":subQ0}),-1.0]])]});}
            var Q5;
            {var subQ5=sQuery(id+"F0.wireOp",EDGE,"E10.1.0");Q5=makeQuery(id+"F0.imprint","IMPRINT",FACE,{"disambiguationData":[TD([[makeQuery(id+"F0.imprint","IMPRINT",EDGE,{"derivedFrom":subQ5}),1.0]])]});}
            var Q6;
            {var subQ1=sQuery(id+"F0.wireOp",EDGE,"E11");Q6=makeQuery(id+"F0.imprint","IMPRINT",FACE,{"disambiguationData":[TD([[makeQuery(id+"F0.imprint","IMPRINT",EDGE,{"derivedFrom":subQ1}),-1.0]])]});}
            var Q7;
            {var subQ2=sQuery(id+"F0.wireOp",EDGE,"E2");Q7=makeQuery(id+"F0.imprint","IMPRINT",FACE,{"disambiguationData":[TD([[makeQuery(id+"F0.imprint","IMPRINT",EDGE,{"derivedFrom":subQ2}),1.0]])]});}
            var Q8;
            {var subQ0=sQuery(id+"F0.wireOp",EDGE,"E12.3.0");Q8=makeQuery(id+"F0.imprint","IMPRINT",FACE,{"disambiguationData":[TD([[makeQuery(id+"F0.imprint","IMPRINT",EDGE,{"derivedFrom":subQ0}),-1.0]])]});}
            extrude(context, id + "F7", {"entities" : qUnion([Q0, Q1, Q2, Q3, Q4, Q5, Q6, Q7, Q8]), "depth" : 0.5 * mm});
        }
        {
            var Q0;
            {var subQ6=sQuery(id+"F0.wireOp",EDGE,"E0");Q0=makeQuery(id+"F0.imprint","IMPRINT",FACE,{"disambiguationData":[TD([[makeQuery(id+"F0.imprint","IMPRINT",EDGE,{"derivedFrom":subQ6}),-1.0]])]});}
            var Q1;
            {var subQ5=sQuery(id+"F0.wireOp",EDGE,"E10.2.0");Q1=makeQuery(id+"F0.imprint","IMPRINT",FACE,{"disambiguationData":[TD([[makeQuery(id+"F0.imprint","IMPRINT",EDGE,{"derivedFrom":subQ5}),1.0]])]});}
            var Q2;
            {var subQ0=sQuery(id+"F0.wireOp",EDGE,"E12.1.0");Q2=makeQuery(id+"F0.imprint","IMPRINT",FACE,{"disambiguationData":[TD([[makeQuery(id+"F0.imprint","IMPRINT",EDGE,{"derivedFrom":subQ0}),-1.0]])]});}
            var Q3;
            {var subQ5=sQuery(id+"F0.wireOp",EDGE,"E10.1.0");Q3=makeQuery(id+"F0.imprint","IMPRINT",FACE,{"disambiguationData":[TD([[makeQuery(id+"F0.imprint","IMPRINT",EDGE,{"derivedFrom":subQ5}),1.0]])]});}
            var Q4;
            {var subQ1=sQuery(id+"F0.wireOp",EDGE,"E11");Q4=makeQuery(id+"F0.imprint","IMPRINT",FACE,{"disambiguationData":[TD([[makeQuery(id+"F0.imprint","IMPRINT",EDGE,{"derivedFrom":subQ1}),-1.0]])]});}
            var Q5;
            {var subQ2=sQuery(id+"F0.wireOp",EDGE,"E2");Q5=makeQuery(id+"F0.imprint","IMPRINT",FACE,{"disambiguationData":[TD([[makeQuery(id+"F0.imprint","IMPRINT",EDGE,{"derivedFrom":subQ2}),1.0]])]});}
            var Q6;
            {var subQ0=sQuery(id+"F0.wireOp",EDGE,"E12.2.0");Q6=makeQuery(id+"F0.imprint","IMPRINT",FACE,{"disambiguationData":[TD([[makeQuery(id+"F0.imprint","IMPRINT",EDGE,{"derivedFrom":subQ0}),-1.0]])]});}
            extrude(context, id + "F8", {"entities" : qUnion([Q0, Q1, Q2, Q3, Q4, Q5, Q6]), "depth" : 0.5 * mm});
        }
        {
            var Q0;
            {var subQ6=sQuery(id+"F0.wireOp",EDGE,"E0");Q0=makeQuery(id+"F0.imprint","IMPRINT",FACE,{"disambiguationData":[TD([[makeQuery(id+"F0.imprint","IMPRINT",EDGE,{"derivedFrom":subQ6}),-1.0]])]});}
            var Q1;
            {var subQ5=sQuery(id+"F0.wireOp",EDGE,"E10.1.0");Q1=makeQuery(id+"F0.imprint","IMPRINT",FACE,{"disambiguationData":[TD([[makeQuery(id+"F0.imprint","IMPRINT",EDGE,{"derivedFrom":subQ5}),1.0]])]});}
            var Q2;
            {var subQ1=sQuery(id+"F0.wireOp",EDGE,"E11");Q2=makeQuery(id+"F0.imprint","IMPRINT",FACE,{"disambiguationData":[TD([[makeQuery(id+"F0.imprint","IMPRINT",EDGE,{"derivedFrom":subQ1}),-1.0]])]});}
            var Q3;
            {var subQ2=sQuery(id+"F0.wireOp",EDGE,"E2");Q3=makeQuery(id+"F0.imprint","IMPRINT",FACE,{"disambiguationData":[TD([[makeQuery(id+"F0.imprint","IMPRINT",EDGE,{"derivedFrom":subQ2}),1.0]])]});}
            var Q4;
            {var subQ0=sQuery(id+"F0.wireOp",EDGE,"E12.1.0");Q4=makeQuery(id+"F0.imprint","IMPRINT",FACE,{"disambiguationData":[TD([[makeQuery(id+"F0.imprint","IMPRINT",EDGE,{"derivedFrom":subQ0}),-1.0]])]});}
            extrude(context, id + "F9", {"entities" : qUnion([Q0, Q1, Q2, Q3, Q4]), "depth" : 0.5 * mm});
        }
        {
            var Q0;
            {var subQ6=sQuery(id+"F0.wireOp",EDGE,"E0");Q0=makeQuery(id+"F0.imprint","IMPRINT",FACE,{"disambiguationData":[TD([[makeQuery(id+"F0.imprint","IMPRINT",EDGE,{"derivedFrom":subQ6}),-1.0]])]});}
            var Q1;
            {var subQ2=sQuery(id+"F0.wireOp",EDGE,"E2");Q1=makeQuery(id+"F0.imprint","IMPRINT",FACE,{"disambiguationData":[TD([[makeQuery(id+"F0.imprint","IMPRINT",EDGE,{"derivedFrom":subQ2}),1.0]])]});}
            var Q2;
            {var subQ1=sQuery(id+"F0.wireOp",EDGE,"E11");Q2=makeQuery(id+"F0.imprint","IMPRINT",FACE,{"disambiguationData":[TD([[makeQuery(id+"F0.imprint","IMPRINT",EDGE,{"derivedFrom":subQ1}),-1.0]])]});}
            extrude(context, id + "F10", {"entities" : qUnion([Q0, Q1, Q2]), "depth" : 0.5 * mm});
        }
        {
            var Q0;
            {var subQ5=sQuery(id+"F0.wireOp",EDGE,"E10.1.0");Q0=makeQuery(id+"F0.imprint","IMPRINT",FACE,{"disambiguationData":[TD([[makeQuery(id+"F0.imprint","IMPRINT",EDGE,{"derivedFrom":subQ5}),1.0]])]});}
            var Q1;
            {var subQ0=sQuery(id+"F0.wireOp",EDGE,"E12.1.0");Q1=makeQuery(id+"F0.imprint","IMPRINT",FACE,{"disambiguationData":[TD([[makeQuery(id+"F0.imprint","IMPRINT",EDGE,{"derivedFrom":subQ0}),-1.0]])]});}
            var Q2;
            {var subQ6=sQuery(id+"F0.wireOp",EDGE,"E0");Q2=makeQuery(id+"F0.imprint","IMPRINT",FACE,{"disambiguationData":[TD([[makeQuery(id+"F0.imprint","IMPRINT",EDGE,{"derivedFrom":subQ6}),-1.0]])]});}
            extrude(context, id + "F11", {"entities" : qUnion([Q0, Q1, Q2]), "depth" : 0.5 * mm});
        }
        {
            var Q0;
            {var subQ5=sQuery(id+"F0.wireOp",EDGE,"E10.1.0");Q0=makeQuery(id+"F0.imprint","IMPRINT",FACE,{"disambiguationData":[TD([[makeQuery(id+"F0.imprint","IMPRINT",EDGE,{"derivedFrom":subQ5}),1.0]])]});}
            var Q1;
            {var subQ6=sQuery(id+"F0.wireOp",EDGE,"E0");Q1=makeQuery(id+"F0.imprint","IMPRINT",FACE,{"disambiguationData":[TD([[makeQuery(id+"F0.imprint","IMPRINT",EDGE,{"derivedFrom":subQ6}),-1.0]])]});}
            var Q2;
            {var subQ5=sQuery(id+"F0.wireOp",EDGE,"E10.2.0");Q2=makeQuery(id+"F0.imprint","IMPRINT",FACE,{"disambiguationData":[TD([[makeQuery(id+"F0.imprint","IMPRINT",EDGE,{"derivedFrom":subQ5}),1.0]])]});}
            var Q3;
            {var subQ5=sQuery(id+"F0.wireOp",EDGE,"E10.3.0");Q3=makeQuery(id+"F0.imprint","IMPRINT",FACE,{"disambiguationData":[TD([[makeQuery(id+"F0.imprint","IMPRINT",EDGE,{"derivedFrom":subQ5}),1.0]])]});}
            var Q4;
            {var subQ5=sQuery(id+"F0.wireOp",EDGE,"E10.4.0");Q4=makeQuery(id+"F0.imprint","IMPRINT",FACE,{"disambiguationData":[TD([[makeQuery(id+"F0.imprint","IMPRINT",EDGE,{"derivedFrom":subQ5}),1.0]])]});}
            var Q5;
            {var subQ5=sQuery(id+"F0.wireOp",EDGE,"E10.5.0");Q5=makeQuery(id+"F0.imprint","IMPRINT",FACE,{"disambiguationData":[TD([[makeQuery(id+"F0.imprint","IMPRINT",EDGE,{"derivedFrom":subQ5}),1.0]])]});}
            var Q6;
            {var subQ5=sQuery(id+"F0.wireOp",EDGE,"E10.6.0");Q6=makeQuery(id+"F0.imprint","IMPRINT",FACE,{"disambiguationData":[TD([[makeQuery(id+"F0.imprint","IMPRINT",EDGE,{"derivedFrom":subQ5}),1.0]])]});}
            var Q7;
            {var subQ5=sQuery(id+"F0.wireOp",EDGE,"E10.7.0");Q7=makeQuery(id+"F0.imprint","IMPRINT",FACE,{"disambiguationData":[TD([[makeQuery(id+"F0.imprint","IMPRINT",EDGE,{"derivedFrom":subQ5}),1.0]])]});}
            var Q8;
            {var subQ5=sQuery(id+"F0.wireOp",EDGE,"E10.8.0");Q8=makeQuery(id+"F0.imprint","IMPRINT",FACE,{"disambiguationData":[TD([[makeQuery(id+"F0.imprint","IMPRINT",EDGE,{"derivedFrom":subQ5}),1.0]])]});}
            var Q9;
            {var subQ1=sQuery(id+"F0.wireOp",EDGE,"E10.9.0");Q9=makeQuery(id+"F0.imprint","IMPRINT",FACE,{"disambiguationData":[TD([[makeQuery(id+"F0.imprint","IMPRINT",EDGE,{"derivedFrom":subQ1}),1.0]])]});}
            var Q10;
            {var subQ0=sQuery(id+"F0.wireOp",EDGE,"E12.8.0");Q10=makeQuery(id+"F0.imprint","IMPRINT",FACE,{"disambiguationData":[TD([[makeQuery(id+"F0.imprint","IMPRINT",EDGE,{"derivedFrom":subQ0}),-1.0]])]});}
            var Q11;
            {var subQ0=sQuery(id+"F0.wireOp",EDGE,"E12.7.0");Q11=makeQuery(id+"F0.imprint","IMPRINT",FACE,{"disambiguationData":[TD([[makeQuery(id+"F0.imprint","IMPRINT",EDGE,{"derivedFrom":subQ0}),-1.0]])]});}
            var Q12;
            {var subQ0=sQuery(id+"F0.wireOp",EDGE,"E12.6.0");Q12=makeQuery(id+"F0.imprint","IMPRINT",FACE,{"disambiguationData":[TD([[makeQuery(id+"F0.imprint","IMPRINT",EDGE,{"derivedFrom":subQ0}),-1.0]])]});}
            var Q13;
            {var subQ0=sQuery(id+"F0.wireOp",EDGE,"E12.5.0");Q13=makeQuery(id+"F0.imprint","IMPRINT",FACE,{"disambiguationData":[TD([[makeQuery(id+"F0.imprint","IMPRINT",EDGE,{"derivedFrom":subQ0}),-1.0]])]});}
            var Q14;
            {var subQ0=sQuery(id+"F0.wireOp",EDGE,"E12.4.0");Q14=makeQuery(id+"F0.imprint","IMPRINT",FACE,{"disambiguationData":[TD([[makeQuery(id+"F0.imprint","IMPRINT",EDGE,{"derivedFrom":subQ0}),-1.0]])]});}
            var Q15;
            {var subQ0=sQuery(id+"F0.wireOp",EDGE,"E12.3.0");Q15=makeQuery(id+"F0.imprint","IMPRINT",FACE,{"disambiguationData":[TD([[makeQuery(id+"F0.imprint","IMPRINT",EDGE,{"derivedFrom":subQ0}),-1.0]])]});}
            var Q16;
            {var subQ0=sQuery(id+"F0.wireOp",EDGE,"E12.2.0");Q16=makeQuery(id+"F0.imprint","IMPRINT",FACE,{"disambiguationData":[TD([[makeQuery(id+"F0.imprint","IMPRINT",EDGE,{"derivedFrom":subQ0}),-1.0]])]});}
            var Q17;
            {var subQ0=sQuery(id+"F0.wireOp",EDGE,"E12.1.0");Q17=makeQuery(id+"F0.imprint","IMPRINT",FACE,{"disambiguationData":[TD([[makeQuery(id+"F0.imprint","IMPRINT",EDGE,{"derivedFrom":subQ0}),-1.0]])]});}
            extrude(context, id + "F12", {"entities" : qUnion([Q0, Q1, Q2, Q3, Q4, Q5, Q6, Q7, Q8, Q9, Q10, Q11, Q12, Q13, Q14, Q15, Q16, Q17]), "depth" : 0.5 * mm});
        }
        {
            var Q0;
            Q0=makeQuery(id+"F1.opExtrude","SWEPT_BODY",BODY,{"disambiguationData":[OSD([sQuery(id+"F0.wireOp",EDGE,"E0"),sQuery(id+"F0.wireOp",EDGE,"E1"),sQuery(id+"F0.wireOp",EDGE,"E2"),sQuery(id+"F0.wireOp",EDGE,"E3"),sQuery(id+"F0.wireOp",EDGE,"E4"),sQuery(id+"F0.wireOp",EDGE,"E5"),sQuery(id+"F0.wireOp",EDGE,"E7"),sQuery(id+"F0.wireOp",EDGE,"E8"),sQuery(id+"F0.wireOp",EDGE,"E10.1.0"),sQuery(id+"F0.wireOp",EDGE,"E10.1.1"),sQuery(id+"F0.wireOp",EDGE,"E10.1.2"),sQuery(id+"F0.wireOp",EDGE,"E10.2.0"),sQuery(id+"F0.wireOp",EDGE,"E10.2.1"),sQuery(id+"F0.wireOp",EDGE,"E10.2.2"),sQuery(id+"F0.wireOp",EDGE,"E10.3.0"),sQuery(id+"F0.wireOp",EDGE,"E10.3.1"),sQuery(id+"F0.wireOp",EDGE,"E10.3.2"),sQuery(id+"F0.wireOp",EDGE,"E10.4.0"),sQuery(id+"F0.wireOp",EDGE,"E10.4.1"),sQuery(id+"F0.wireOp",EDGE,"E10.4.2"),sQuery(id+"F0.wireOp",EDGE,"E10.5.0"),sQuery(id+"F0.wireOp",EDGE,"E10.5.1"),sQuery(id+"F0.wireOp",EDGE,"E10.5.2"),sQuery(id+"F0.wireOp",EDGE,"E10.6.0"),sQuery(id+"F0.wireOp",EDGE,"E10.6.1"),sQuery(id+"F0.wireOp",EDGE,"E10.6.2"),sQuery(id+"F0.wireOp",EDGE,"E10.7.0"),sQuery(id+"F0.wireOp",EDGE,"E10.7.1"),sQuery(id+"F0.wireOp",EDGE,"E10.7.2"),sQuery(id+"F0.wireOp",EDGE,"E10.8.0"),sQuery(id+"F0.wireOp",EDGE,"E10.8.1"),sQuery(id+"F0.wireOp",EDGE,"E10.8.2"),sQuery(id+"F0.wireOp",EDGE,"E10.9.0"),sQuery(id+"F0.wireOp",EDGE,"E10.9.1"),sQuery(id+"F0.wireOp",EDGE,"E10.9.2"),sQuery(id+"F0.wireOp",EDGE,"E11"),sQuery(id+"F0.wireOp",EDGE,"E12.1.0"),sQuery(id+"F0.wireOp",EDGE,"E12.2.0"),sQuery(id+"F0.wireOp",EDGE,"E12.3.0"),sQuery(id+"F0.wireOp",EDGE,"E12.4.0"),sQuery(id+"F0.wireOp",EDGE,"E12.5.0"),sQuery(id+"F0.wireOp",EDGE,"E12.6.0"),sQuery(id+"F0.wireOp",EDGE,"E12.7.0"),sQuery(id+"F0.wireOp",EDGE,"E12.8.0"),sQuery(id+"F0.wireOp",EDGE,"E14"),sQuery(id+"F0.wireOp",EDGE,"E16"),sQuery(id+"F0.wireOp",EDGE,"E17"),sQuery(id+"F0.wireOp",EDGE,"E18"),sQuery(id+"F0.wireOp",EDGE,"E19"),sQuery(id+"F0.wireOp",EDGE,"E20.trimOffspring"),sQuery(id+"F0.wireOp",EDGE,"E21.trimOffspring"),sQuery(id+"F0.wireOp",EDGE,"E23"),sQuery(id+"F0.wireOp",EDGE,"E24")])]});
            var Q1;
            Q1=makeQuery(id+"F2.opExtrude","SWEPT_BODY",BODY,{"disambiguationData":[OSD([sQuery(id+"F0.wireOp",EDGE,"E0"),sQuery(id+"F0.wireOp",EDGE,"E1"),sQuery(id+"F0.wireOp",EDGE,"E2"),sQuery(id+"F0.wireOp",EDGE,"E3"),sQuery(id+"F0.wireOp",EDGE,"E4"),sQuery(id+"F0.wireOp",EDGE,"E5"),sQuery(id+"F0.wireOp",EDGE,"E7"),sQuery(id+"F0.wireOp",EDGE,"E8"),sQuery(id+"F0.wireOp",EDGE,"E10.1.0"),sQuery(id+"F0.wireOp",EDGE,"E10.1.1"),sQuery(id+"F0.wireOp",EDGE,"E10.1.2"),sQuery(id+"F0.wireOp",EDGE,"E10.2.0"),sQuery(id+"F0.wireOp",EDGE,"E10.2.1"),sQuery(id+"F0.wireOp",EDGE,"E10.2.2"),sQuery(id+"F0.wireOp",EDGE,"E10.3.0"),sQuery(id+"F0.wireOp",EDGE,"E10.3.1"),sQuery(id+"F0.wireOp",EDGE,"E10.3.2"),sQuery(id+"F0.wireOp",EDGE,"E10.4.0"),sQuery(id+"F0.wireOp",EDGE,"E10.4.1"),sQuery(id+"F0.wireOp",EDGE,"E10.4.2"),sQuery(id+"F0.wireOp",EDGE,"E10.5.0"),sQuery(id+"F0.wireOp",EDGE,"E10.5.1"),sQuery(id+"F0.wireOp",EDGE,"E10.5.2"),sQuery(id+"F0.wireOp",EDGE,"E10.6.0"),sQuery(id+"F0.wireOp",EDGE,"E10.6.1"),sQuery(id+"F0.wireOp",EDGE,"E10.6.2"),sQuery(id+"F0.wireOp",EDGE,"E10.7.0"),sQuery(id+"F0.wireOp",EDGE,"E10.7.1"),sQuery(id+"F0.wireOp",EDGE,"E10.7.2"),sQuery(id+"F0.wireOp",EDGE,"E10.8.0"),sQuery(id+"F0.wireOp",EDGE,"E10.8.1"),sQuery(id+"F0.wireOp",EDGE,"E10.8.2"),sQuery(id+"F0.wireOp",EDGE,"E11"),sQuery(id+"F0.wireOp",EDGE,"E12.1.0"),sQuery(id+"F0.wireOp",EDGE,"E12.2.0"),sQuery(id+"F0.wireOp",EDGE,"E12.3.0"),sQuery(id+"F0.wireOp",EDGE,"E12.4.0"),sQuery(id+"F0.wireOp",EDGE,"E12.5.0"),sQuery(id+"F0.wireOp",EDGE,"E12.6.0"),sQuery(id+"F0.wireOp",EDGE,"E12.7.0"),sQuery(id+"F0.wireOp",EDGE,"E12.8.0"),sQuery(id+"F0.wireOp",EDGE,"E14"),sQuery(id+"F0.wireOp",EDGE,"E16"),sQuery(id+"F0.wireOp",EDGE,"E17"),sQuery(id+"F0.wireOp",EDGE,"E18"),sQuery(id+"F0.wireOp",EDGE,"E19"),sQuery(id+"F0.wireOp",EDGE,"E20.trimOffspring"),sQuery(id+"F0.wireOp",EDGE,"E21.trimOffspring"),sQuery(id+"F0.wireOp",EDGE,"E23"),sQuery(id+"F0.wireOp",EDGE,"E24")])]});
            var Q2;
            Q2=makeQuery(id+"F3.opExtrude","SWEPT_BODY",BODY,{"disambiguationData":[OSD([sQuery(id+"F0.wireOp",EDGE,"E0"),sQuery(id+"F0.wireOp",EDGE,"E1"),sQuery(id+"F0.wireOp",EDGE,"E2"),sQuery(id+"F0.wireOp",EDGE,"E3"),sQuery(id+"F0.wireOp",EDGE,"E4"),sQuery(id+"F0.wireOp",EDGE,"E5"),sQuery(id+"F0.wireOp",EDGE,"E7"),sQuery(id+"F0.wireOp",EDGE,"E8"),sQuery(id+"F0.wireOp",EDGE,"E10.1.0"),sQuery(id+"F0.wireOp",EDGE,"E10.1.1"),sQuery(id+"F0.wireOp",EDGE,"E10.1.2"),sQuery(id+"F0.wireOp",EDGE,"E10.2.0"),sQuery(id+"F0.wireOp",EDGE,"E10.2.1"),sQuery(id+"F0.wireOp",EDGE,"E10.2.2"),sQuery(id+"F0.wireOp",EDGE,"E10.3.0"),sQuery(id+"F0.wireOp",EDGE,"E10.3.1"),sQuery(id+"F0.wireOp",EDGE,"E10.3.2"),sQuery(id+"F0.wireOp",EDGE,"E10.4.0"),sQuery(id+"F0.wireOp",EDGE,"E10.4.1"),sQuery(id+"F0.wireOp",EDGE,"E10.4.2"),sQuery(id+"F0.wireOp",EDGE,"E10.5.0"),sQuery(id+"F0.wireOp",EDGE,"E10.5.1"),sQuery(id+"F0.wireOp",EDGE,"E10.5.2"),sQuery(id+"F0.wireOp",EDGE,"E10.6.0"),sQuery(id+"F0.wireOp",EDGE,"E10.6.1"),sQuery(id+"F0.wireOp",EDGE,"E10.6.2"),sQuery(id+"F0.wireOp",EDGE,"E10.7.0"),sQuery(id+"F0.wireOp",EDGE,"E10.7.1"),sQuery(id+"F0.wireOp",EDGE,"E10.7.2"),sQuery(id+"F0.wireOp",EDGE,"E11"),sQuery(id+"F0.wireOp",EDGE,"E12.1.0"),sQuery(id+"F0.wireOp",EDGE,"E12.2.0"),sQuery(id+"F0.wireOp",EDGE,"E12.3.0"),sQuery(id+"F0.wireOp",EDGE,"E12.4.0"),sQuery(id+"F0.wireOp",EDGE,"E12.5.0"),sQuery(id+"F0.wireOp",EDGE,"E12.6.0"),sQuery(id+"F0.wireOp",EDGE,"E12.7.0"),sQuery(id+"F0.wireOp",EDGE,"E14"),sQuery(id+"F0.wireOp",EDGE,"E16"),sQuery(id+"F0.wireOp",EDGE,"E17"),sQuery(id+"F0.wireOp",EDGE,"E18"),sQuery(id+"F0.wireOp",EDGE,"E19"),sQuery(id+"F0.wireOp",EDGE,"E20.trimOffspring"),sQuery(id+"F0.wireOp",EDGE,"E21.trimOffspring"),sQuery(id+"F0.wireOp",EDGE,"E23"),sQuery(id+"F0.wireOp",EDGE,"E24")])]});
            var Q3;
            Q3=makeQuery(id+"F4.opExtrude","SWEPT_BODY",BODY,{"disambiguationData":[OSD([sQuery(id+"F0.wireOp",EDGE,"E0"),sQuery(id+"F0.wireOp",EDGE,"E1"),sQuery(id+"F0.wireOp",EDGE,"E2"),sQuery(id+"F0.wireOp",EDGE,"E3"),sQuery(id+"F0.wireOp",EDGE,"E4"),sQuery(id+"F0.wireOp",EDGE,"E5"),sQuery(id+"F0.wireOp",EDGE,"E7"),sQuery(id+"F0.wireOp",EDGE,"E8"),sQuery(id+"F0.wireOp",EDGE,"E10.1.0"),sQuery(id+"F0.wireOp",EDGE,"E10.1.1"),sQuery(id+"F0.wireOp",EDGE,"E10.1.2"),sQuery(id+"F0.wireOp",EDGE,"E10.2.0"),sQuery(id+"F0.wireOp",EDGE,"E10.2.1"),sQuery(id+"F0.wireOp",EDGE,"E10.2.2"),sQuery(id+"F0.wireOp",EDGE,"E10.3.0"),sQuery(id+"F0.wireOp",EDGE,"E10.3.1"),sQuery(id+"F0.wireOp",EDGE,"E10.3.2"),sQuery(id+"F0.wireOp",EDGE,"E10.4.0"),sQuery(id+"F0.wireOp",EDGE,"E10.4.1"),sQuery(id+"F0.wireOp",EDGE,"E10.4.2"),sQuery(id+"F0.wireOp",EDGE,"E10.5.0"),sQuery(id+"F0.wireOp",EDGE,"E10.5.1"),sQuery(id+"F0.wireOp",EDGE,"E10.5.2"),sQuery(id+"F0.wireOp",EDGE,"E10.6.0"),sQuery(id+"F0.wireOp",EDGE,"E10.6.1"),sQuery(id+"F0.wireOp",EDGE,"E10.6.2"),sQuery(id+"F0.wireOp",EDGE,"E11"),sQuery(id+"F0.wireOp",EDGE,"E12.1.0"),sQuery(id+"F0.wireOp",EDGE,"E12.2.0"),sQuery(id+"F0.wireOp",EDGE,"E12.3.0"),sQuery(id+"F0.wireOp",EDGE,"E12.4.0"),sQuery(id+"F0.wireOp",EDGE,"E12.5.0"),sQuery(id+"F0.wireOp",EDGE,"E12.6.0"),sQuery(id+"F0.wireOp",EDGE,"E14"),sQuery(id+"F0.wireOp",EDGE,"E16"),sQuery(id+"F0.wireOp",EDGE,"E17"),sQuery(id+"F0.wireOp",EDGE,"E18"),sQuery(id+"F0.wireOp",EDGE,"E19"),sQuery(id+"F0.wireOp",EDGE,"E20.trimOffspring"),sQuery(id+"F0.wireOp",EDGE,"E21.trimOffspring"),sQuery(id+"F0.wireOp",EDGE,"E23"),sQuery(id+"F0.wireOp",EDGE,"E24")])]});
            var Q4;
            Q4=makeQuery(id+"F5.opExtrude","SWEPT_BODY",BODY,{"disambiguationData":[OSD([sQuery(id+"F0.wireOp",EDGE,"E0"),sQuery(id+"F0.wireOp",EDGE,"E1"),sQuery(id+"F0.wireOp",EDGE,"E2"),sQuery(id+"F0.wireOp",EDGE,"E3"),sQuery(id+"F0.wireOp",EDGE,"E4"),sQuery(id+"F0.wireOp",EDGE,"E5"),sQuery(id+"F0.wireOp",EDGE,"E7"),sQuery(id+"F0.wireOp",EDGE,"E8"),sQuery(id+"F0.wireOp",EDGE,"E10.1.0"),sQuery(id+"F0.wireOp",EDGE,"E10.1.1"),sQuery(id+"F0.wireOp",EDGE,"E10.1.2"),sQuery(id+"F0.wireOp",EDGE,"E10.2.0"),sQuery(id+"F0.wireOp",EDGE,"E10.2.1"),sQuery(id+"F0.wireOp",EDGE,"E10.2.2"),sQuery(id+"F0.wireOp",EDGE,"E10.3.0"),sQuery(id+"F0.wireOp",EDGE,"E10.3.1"),sQuery(id+"F0.wireOp",EDGE,"E10.3.2"),sQuery(id+"F0.wireOp",EDGE,"E10.4.0"),sQuery(id+"F0.wireOp",EDGE,"E10.4.1"),sQuery(id+"F0.wireOp",EDGE,"E10.4.2"),sQuery(id+"F0.wireOp",EDGE,"E10.5.0"),sQuery(id+"F0.wireOp",EDGE,"E10.5.1"),sQuery(id+"F0.wireOp",EDGE,"E10.5.2"),sQuery(id+"F0.wireOp",EDGE,"E11"),sQuery(id+"F0.wireOp",EDGE,"E12.1.0"),sQuery(id+"F0.wireOp",EDGE,"E12.2.0"),sQuery(id+"F0.wireOp",EDGE,"E12.3.0"),sQuery(id+"F0.wireOp",EDGE,"E12.4.0"),sQuery(id+"F0.wireOp",EDGE,"E12.5.0"),sQuery(id+"F0.wireOp",EDGE,"E14"),sQuery(id+"F0.wireOp",EDGE,"E16"),sQuery(id+"F0.wireOp",EDGE,"E17"),sQuery(id+"F0.wireOp",EDGE,"E18"),sQuery(id+"F0.wireOp",EDGE,"E19"),sQuery(id+"F0.wireOp",EDGE,"E20.trimOffspring"),sQuery(id+"F0.wireOp",EDGE,"E21.trimOffspring"),sQuery(id+"F0.wireOp",EDGE,"E23"),sQuery(id+"F0.wireOp",EDGE,"E24")])]});
            var Q5;
            Q5=makeQuery(id+"F6.opExtrude","SWEPT_BODY",BODY,{"disambiguationData":[OSD([sQuery(id+"F0.wireOp",EDGE,"E0"),sQuery(id+"F0.wireOp",EDGE,"E1"),sQuery(id+"F0.wireOp",EDGE,"E2"),sQuery(id+"F0.wireOp",EDGE,"E3"),sQuery(id+"F0.wireOp",EDGE,"E4"),sQuery(id+"F0.wireOp",EDGE,"E5"),sQuery(id+"F0.wireOp",EDGE,"E7"),sQuery(id+"F0.wireOp",EDGE,"E8"),sQuery(id+"F0.wireOp",EDGE,"E10.1.0"),sQuery(id+"F0.wireOp",EDGE,"E10.1.1"),sQuery(id+"F0.wireOp",EDGE,"E10.1.2"),sQuery(id+"F0.wireOp",EDGE,"E10.2.0"),sQuery(id+"F0.wireOp",EDGE,"E10.2.1"),sQuery(id+"F0.wireOp",EDGE,"E10.2.2"),sQuery(id+"F0.wireOp",EDGE,"E10.3.0"),sQuery(id+"F0.wireOp",EDGE,"E10.3.1"),sQuery(id+"F0.wireOp",EDGE,"E10.3.2"),sQuery(id+"F0.wireOp",EDGE,"E10.4.0"),sQuery(id+"F0.wireOp",EDGE,"E10.4.1"),sQuery(id+"F0.wireOp",EDGE,"E10.4.2"),sQuery(id+"F0.wireOp",EDGE,"E11"),sQuery(id+"F0.wireOp",EDGE,"E12.1.0"),sQuery(id+"F0.wireOp",EDGE,"E12.2.0"),sQuery(id+"F0.wireOp",EDGE,"E12.3.0"),sQuery(id+"F0.wireOp",EDGE,"E12.4.0"),sQuery(id+"F0.wireOp",EDGE,"E14"),sQuery(id+"F0.wireOp",EDGE,"E16"),sQuery(id+"F0.wireOp",EDGE,"E17"),sQuery(id+"F0.wireOp",EDGE,"E18"),sQuery(id+"F0.wireOp",EDGE,"E19"),sQuery(id+"F0.wireOp",EDGE,"E20.trimOffspring"),sQuery(id+"F0.wireOp",EDGE,"E21.trimOffspring"),sQuery(id+"F0.wireOp",EDGE,"E23"),sQuery(id+"F0.wireOp",EDGE,"E24")])]});
            var Q6;
            Q6=makeQuery(id+"F7.opExtrude","SWEPT_BODY",BODY,{"disambiguationData":[OSD([sQuery(id+"F0.wireOp",EDGE,"E0"),sQuery(id+"F0.wireOp",EDGE,"E1"),sQuery(id+"F0.wireOp",EDGE,"E2"),sQuery(id+"F0.wireOp",EDGE,"E3"),sQuery(id+"F0.wireOp",EDGE,"E4"),sQuery(id+"F0.wireOp",EDGE,"E5"),sQuery(id+"F0.wireOp",EDGE,"E7"),sQuery(id+"F0.wireOp",EDGE,"E8"),sQuery(id+"F0.wireOp",EDGE,"E10.1.0"),sQuery(id+"F0.wireOp",EDGE,"E10.1.1"),sQuery(id+"F0.wireOp",EDGE,"E10.1.2"),sQuery(id+"F0.wireOp",EDGE,"E10.2.0"),sQuery(id+"F0.wireOp",EDGE,"E10.2.1"),sQuery(id+"F0.wireOp",EDGE,"E10.2.2"),sQuery(id+"F0.wireOp",EDGE,"E10.3.0"),sQuery(id+"F0.wireOp",EDGE,"E10.3.1"),sQuery(id+"F0.wireOp",EDGE,"E10.3.2"),sQuery(id+"F0.wireOp",EDGE,"E11"),sQuery(id+"F0.wireOp",EDGE,"E12.1.0"),sQuery(id+"F0.wireOp",EDGE,"E12.2.0"),sQuery(id+"F0.wireOp",EDGE,"E12.3.0"),sQuery(id+"F0.wireOp",EDGE,"E14"),sQuery(id+"F0.wireOp",EDGE,"E16"),sQuery(id+"F0.wireOp",EDGE,"E17"),sQuery(id+"F0.wireOp",EDGE,"E18"),sQuery(id+"F0.wireOp",EDGE,"E19"),sQuery(id+"F0.wireOp",EDGE,"E20.trimOffspring"),sQuery(id+"F0.wireOp",EDGE,"E21.trimOffspring"),sQuery(id+"F0.wireOp",EDGE,"E23"),sQuery(id+"F0.wireOp",EDGE,"E24")])]});
            var Q7;
            Q7=makeQuery(id+"F8.opExtrude","SWEPT_BODY",BODY,{"disambiguationData":[OSD([sQuery(id+"F0.wireOp",EDGE,"E0"),sQuery(id+"F0.wireOp",EDGE,"E1"),sQuery(id+"F0.wireOp",EDGE,"E2"),sQuery(id+"F0.wireOp",EDGE,"E3"),sQuery(id+"F0.wireOp",EDGE,"E4"),sQuery(id+"F0.wireOp",EDGE,"E5"),sQuery(id+"F0.wireOp",EDGE,"E7"),sQuery(id+"F0.wireOp",EDGE,"E8"),sQuery(id+"F0.wireOp",EDGE,"E10.1.0"),sQuery(id+"F0.wireOp",EDGE,"E10.1.1"),sQuery(id+"F0.wireOp",EDGE,"E10.1.2"),sQuery(id+"F0.wireOp",EDGE,"E10.2.0"),sQuery(id+"F0.wireOp",EDGE,"E10.2.1"),sQuery(id+"F0.wireOp",EDGE,"E10.2.2"),sQuery(id+"F0.wireOp",EDGE,"E11"),sQuery(id+"F0.wireOp",EDGE,"E12.1.0"),sQuery(id+"F0.wireOp",EDGE,"E12.2.0"),sQuery(id+"F0.wireOp",EDGE,"E14"),sQuery(id+"F0.wireOp",EDGE,"E16"),sQuery(id+"F0.wireOp",EDGE,"E17"),sQuery(id+"F0.wireOp",EDGE,"E18"),sQuery(id+"F0.wireOp",EDGE,"E19"),sQuery(id+"F0.wireOp",EDGE,"E20.trimOffspring"),sQuery(id+"F0.wireOp",EDGE,"E21.trimOffspring"),sQuery(id+"F0.wireOp",EDGE,"E23"),sQuery(id+"F0.wireOp",EDGE,"E24")])]});
            var Q8;
            Q8=makeQuery(id+"F9.opExtrude","SWEPT_BODY",BODY,{"disambiguationData":[OSD([sQuery(id+"F0.wireOp",EDGE,"E0"),sQuery(id+"F0.wireOp",EDGE,"E1"),sQuery(id+"F0.wireOp",EDGE,"E2"),sQuery(id+"F0.wireOp",EDGE,"E3"),sQuery(id+"F0.wireOp",EDGE,"E4"),sQuery(id+"F0.wireOp",EDGE,"E5"),sQuery(id+"F0.wireOp",EDGE,"E7"),sQuery(id+"F0.wireOp",EDGE,"E8"),sQuery(id+"F0.wireOp",EDGE,"E10.1.0"),sQuery(id+"F0.wireOp",EDGE,"E10.1.1"),sQuery(id+"F0.wireOp",EDGE,"E10.1.2"),sQuery(id+"F0.wireOp",EDGE,"E11"),sQuery(id+"F0.wireOp",EDGE,"E12.1.0"),sQuery(id+"F0.wireOp",EDGE,"E14"),sQuery(id+"F0.wireOp",EDGE,"E16"),sQuery(id+"F0.wireOp",EDGE,"E17"),sQuery(id+"F0.wireOp",EDGE,"E18"),sQuery(id+"F0.wireOp",EDGE,"E19"),sQuery(id+"F0.wireOp",EDGE,"E20.trimOffspring"),sQuery(id+"F0.wireOp",EDGE,"E21.trimOffspring"),sQuery(id+"F0.wireOp",EDGE,"E23"),sQuery(id+"F0.wireOp",EDGE,"E24")])]});
            var Q9;
            Q9=makeQuery(id+"F10.opExtrude","SWEPT_BODY",BODY,{"disambiguationData":[OSD([sQuery(id+"F0.wireOp",EDGE,"E0"),sQuery(id+"F0.wireOp",EDGE,"E1"),sQuery(id+"F0.wireOp",EDGE,"E2"),sQuery(id+"F0.wireOp",EDGE,"E3"),sQuery(id+"F0.wireOp",EDGE,"E4"),sQuery(id+"F0.wireOp",EDGE,"E5"),sQuery(id+"F0.wireOp",EDGE,"E7"),sQuery(id+"F0.wireOp",EDGE,"E8"),sQuery(id+"F0.wireOp",EDGE,"E11"),sQuery(id+"F0.wireOp",EDGE,"E14"),sQuery(id+"F0.wireOp",EDGE,"E16"),sQuery(id+"F0.wireOp",EDGE,"E17"),sQuery(id+"F0.wireOp",EDGE,"E18"),sQuery(id+"F0.wireOp",EDGE,"E19"),sQuery(id+"F0.wireOp",EDGE,"E20.trimOffspring"),sQuery(id+"F0.wireOp",EDGE,"E21.trimOffspring"),sQuery(id+"F0.wireOp",EDGE,"E23"),sQuery(id+"F0.wireOp",EDGE,"E24")])]});
            var Q10;
            Q10=makeQuery(id+"F11.opExtrude","SWEPT_BODY",BODY,{"disambiguationData":[OSD([sQuery(id+"F0.wireOp",EDGE,"E0"),sQuery(id+"F0.wireOp",EDGE,"E1"),sQuery(id+"F0.wireOp",EDGE,"E3"),sQuery(id+"F0.wireOp",EDGE,"E4"),sQuery(id+"F0.wireOp",EDGE,"E5"),sQuery(id+"F0.wireOp",EDGE,"E10.1.0"),sQuery(id+"F0.wireOp",EDGE,"E10.1.1"),sQuery(id+"F0.wireOp",EDGE,"E10.1.2"),sQuery(id+"F0.wireOp",EDGE,"E12.1.0"),sQuery(id+"F0.wireOp",EDGE,"E14"),sQuery(id+"F0.wireOp",EDGE,"E16"),sQuery(id+"F0.wireOp",EDGE,"E17"),sQuery(id+"F0.wireOp",EDGE,"E18"),sQuery(id+"F0.wireOp",EDGE,"E19"),sQuery(id+"F0.wireOp",EDGE,"E20.trimOffspring"),sQuery(id+"F0.wireOp",EDGE,"E21.trimOffspring"),sQuery(id+"F0.wireOp",EDGE,"E23"),sQuery(id+"F0.wireOp",EDGE,"E24")])]});
            var Q11;
            Q11=makeQuery(id+"F12.opExtrude","SWEPT_BODY",BODY,{"disambiguationData":[OSD([sQuery(id+"F0.wireOp",EDGE,"E0"),sQuery(id+"F0.wireOp",EDGE,"E1"),sQuery(id+"F0.wireOp",EDGE,"E3"),sQuery(id+"F0.wireOp",EDGE,"E4"),sQuery(id+"F0.wireOp",EDGE,"E5"),sQuery(id+"F0.wireOp",EDGE,"E10.1.0"),sQuery(id+"F0.wireOp",EDGE,"E10.1.1"),sQuery(id+"F0.wireOp",EDGE,"E10.1.2"),sQuery(id+"F0.wireOp",EDGE,"E10.2.0"),sQuery(id+"F0.wireOp",EDGE,"E10.2.1"),sQuery(id+"F0.wireOp",EDGE,"E10.2.2"),sQuery(id+"F0.wireOp",EDGE,"E10.3.0"),sQuery(id+"F0.wireOp",EDGE,"E10.3.1"),sQuery(id+"F0.wireOp",EDGE,"E10.3.2"),sQuery(id+"F0.wireOp",EDGE,"E10.4.0"),sQuery(id+"F0.wireOp",EDGE,"E10.4.1"),sQuery(id+"F0.wireOp",EDGE,"E10.4.2"),sQuery(id+"F0.wireOp",EDGE,"E10.5.0"),sQuery(id+"F0.wireOp",EDGE,"E10.5.1"),sQuery(id+"F0.wireOp",EDGE,"E10.5.2"),sQuery(id+"F0.wireOp",EDGE,"E10.6.0"),sQuery(id+"F0.wireOp",EDGE,"E10.6.1"),sQuery(id+"F0.wireOp",EDGE,"E10.6.2"),sQuery(id+"F0.wireOp",EDGE,"E10.7.0"),sQuery(id+"F0.wireOp",EDGE,"E10.7.1"),sQuery(id+"F0.wireOp",EDGE,"E10.7.2"),sQuery(id+"F0.wireOp",EDGE,"E10.8.0"),sQuery(id+"F0.wireOp",EDGE,"E10.8.1"),sQuery(id+"F0.wireOp",EDGE,"E10.8.2"),sQuery(id+"F0.wireOp",EDGE,"E10.9.0"),sQuery(id+"F0.wireOp",EDGE,"E10.9.1"),sQuery(id+"F0.wireOp",EDGE,"E10.9.2"),sQuery(id+"F0.wireOp",EDGE,"E12.1.0"),sQuery(id+"F0.wireOp",EDGE,"E12.2.0"),sQuery(id+"F0.wireOp",EDGE,"E12.3.0"),sQuery(id+"F0.wireOp",EDGE,"E12.4.0"),sQuery(id+"F0.wireOp",EDGE,"E12.5.0"),sQuery(id+"F0.wireOp",EDGE,"E12.6.0"),sQuery(id+"F0.wireOp",EDGE,"E12.7.0"),sQuery(id+"F0.wireOp",EDGE,"E12.8.0"),sQuery(id+"F0.wireOp",EDGE,"E14"),sQuery(id+"F0.wireOp",EDGE,"E16"),sQuery(id+"F0.wireOp",EDGE,"E17"),sQuery(id+"F0.wireOp",EDGE,"E18"),sQuery(id+"F0.wireOp",EDGE,"E19"),sQuery(id+"F0.wireOp",EDGE,"E20.trimOffspring"),sQuery(id+"F0.wireOp",EDGE,"E21.trimOffspring"),sQuery(id+"F0.wireOp",EDGE,"E23"),sQuery(id+"F0.wireOp",EDGE,"E24")])]});
            var Q12;
            Q12=qCreatedBy(makeId("Origin.pointOp"),VERTEX);
            transform(context, id + "F13", {"entities" : qUnion([Q0, Q1, Q2, Q3, Q4, Q5, Q6, Q7, Q8, Q9, Q10, Q11]), "transformType" : TransformType.SCALE_UNIFORMLY, "scale" : 3, "makeCopy" : false, "scalePoint" : qUnion([Q12])});
        }
    });
